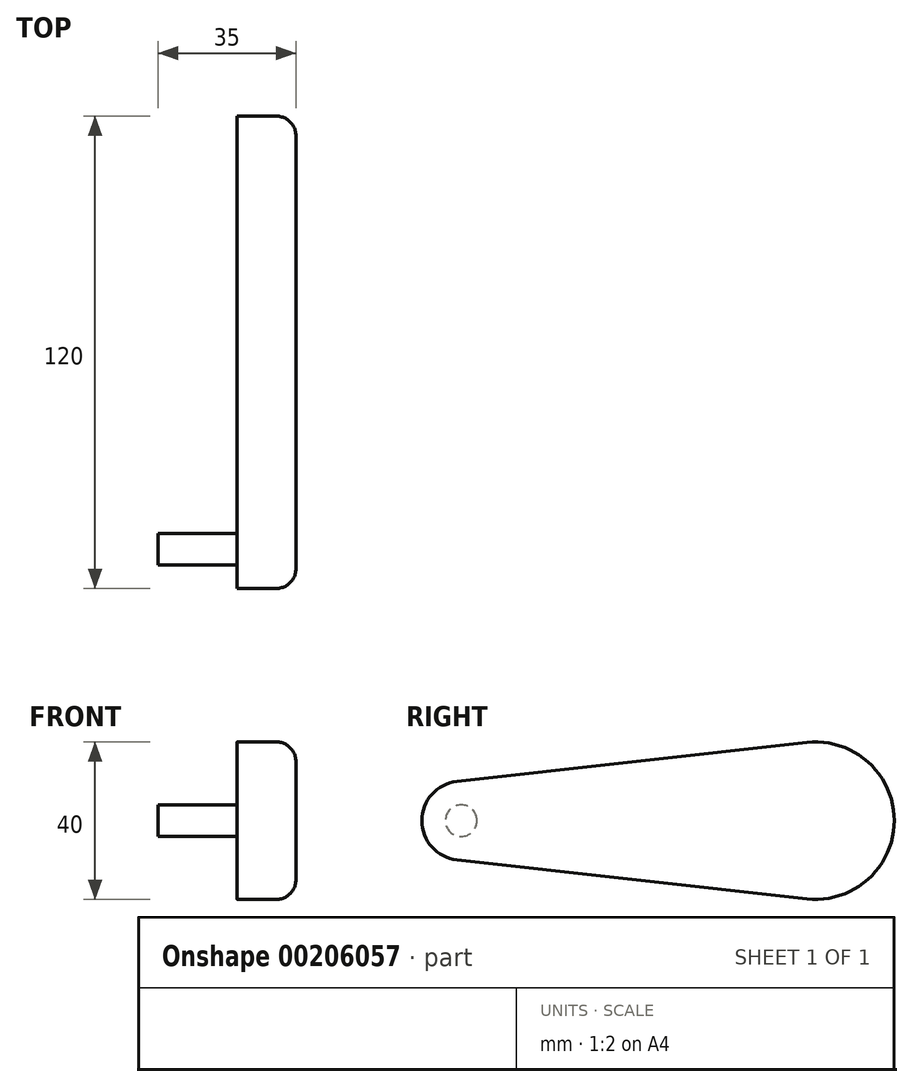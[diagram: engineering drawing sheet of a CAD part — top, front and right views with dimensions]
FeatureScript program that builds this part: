
annotation { "Feature Type Name" : "Feature", "Feature Type Description" : "" }
export const myFeature = defineFeature(function(context is Context, id is Id, definition is map)
    precondition{}
    {
        {
            var Q0;
            Q0=qCreatedBy(makeId("Right.planeOp"),FACE);
            var sketch = newSketch(context, id + "F0", { "sketchPlane" : qUnion([Q0])});
            skCircle(sketch, "E0", {"center": v(0, 0) * mm, "radius": 20 * mm});
            skCircle(sketch, "E1", {"center": v(-90, 0) * mm, "radius": 10 * mm});
            skLineSegment(sketch, "E2", {"start": v(-91.11, 9.94) * mm, "end": v(-2.22, 19.88) * mm});
            skLineSegment(sketch, "E3", {"start": v(-91.11, -9.94) * mm, "end": v(-2.22, -19.88) * mm});
            skSolve(sketch);
        }
        {
            var Q0;
            {var subQ0=sQuery(id+"F0.wireOp",EDGE,"E2");Q0=makeQuery(id+"F0.imprint","IMPRINT",FACE,{"disambiguationData":[TD([[makeQuery(id+"F0.imprint","IMPRINT",EDGE,{"derivedFrom":subQ0}),-1.0]])]});}
            var Q1;
            {var subQ0=sQuery(id+"F0.wireOp",EDGE,"E0");var subQ1=makeQuery(id+"F0.imprint","INTERSECT",VERTEX,{"derivedFrom":[subQ0,sQuery(id+"F0.wireOp",EDGE,"E2")]});Q1=makeQuery(id+"F0.imprint","IMPRINT",FACE,{"disambiguationData":[TD([[makeQuery(id+"F0.imprint","IMPRINT",EDGE,{"disambiguationData":[TD([[subQ1,-1.0]])],"derivedFrom":subQ0}),1.0]])]});}
            var Q2;
            {var subQ0=sQuery(id+"F0.wireOp",EDGE,"E1");var subQ1=makeQuery(id+"F0.imprint","INTERSECT",VERTEX,{"derivedFrom":[subQ0,sQuery(id+"F0.wireOp",EDGE,"E2")]});Q2=makeQuery(id+"F0.imprint","IMPRINT",FACE,{"disambiguationData":[TD([[makeQuery(id+"F0.imprint","IMPRINT",EDGE,{"disambiguationData":[TD([[subQ1,-1.0]])],"derivedFrom":subQ0}),1.0]])]});}
            extrude(context, id + "F1", {"entities" : qUnion([Q0, Q1, Q2]), "depth" : 15 * mm});
        }
        {
            var Q0;
            Q0=qCreatedBy(makeId("Right.planeOp"),FACE);
            var sketch = newSketch(context, id + "F2", { "sketchPlane" : qUnion([Q0])});
            skCircle(sketch, "E4", {"center": v(-90, 0) * mm, "radius": 4 * mm});
            skSolve(sketch);
        }
        {
            var Q0;
            Q0=makeQuery(id+"F2.imprint","IMPRINT",FACE,{"disambiguationData":[TD([[makeQuery(id+"F2.imprint","IMPRINT",EDGE,{"derivedFrom":sQuery(id+"F2.wireOp",EDGE,"E4")}),1.0]])]});
            extrude(context, id + "F3", {"entities" : qUnion([Q0]), "operationType" : NewBodyOperationType.ADD, "oppositeDirection" : true, "depth" : 20 * mm});
        }
        {
            var Q0;
            Q0=makeQuery(id+"F1.opExtrude","CAP_FACE",FACE,{"disambiguationData":[OSD([sQuery(id+"F0.wireOp",EDGE,"E0"),sQuery(id+"F0.wireOp",EDGE,"E1"),sQuery(id+"F0.wireOp",EDGE,"E2"),sQuery(id+"F0.wireOp",EDGE,"E3")])],"isStart":false});
            fillet(context, id + "F4", {"entities" : qUnion([Q0]), "radius" : 5 * mm, "tangentPropagation" : true, "allowEdgeOverflow" : false});
        }
    });
